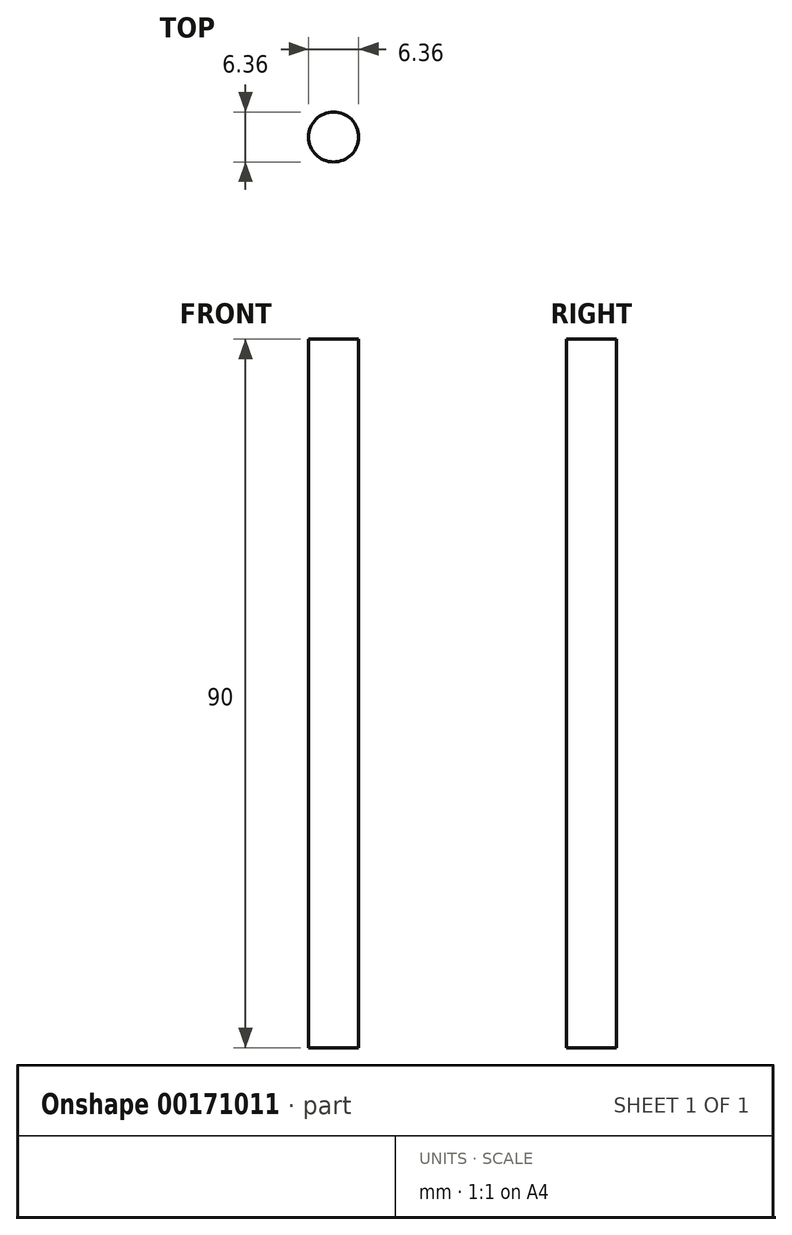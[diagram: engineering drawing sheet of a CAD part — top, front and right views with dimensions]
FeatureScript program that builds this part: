
annotation { "Feature Type Name" : "Feature", "Feature Type Description" : "" }
export const myFeature = defineFeature(function(context is Context, id is Id, definition is map)
    precondition{}
    {
        {
            var Q0;
            Q0=qCreatedBy(makeId("Top.planeOp"),FACE);
            var sketch = newSketch(context, id + "F0", { "sketchPlane" : qUnion([Q0])});
            skCircle(sketch, "E0", {"center": v(0, 0) * mm, "radius": 3.17 * mm});
            skSolve(sketch);
        }
        {
            var Q0;
            Q0=makeQuery(id+"F0.imprint","IMPRINT",FACE,{"disambiguationData":[TD([[makeQuery(id+"F0.imprint","IMPRINT",EDGE,{"derivedFrom":sQuery(id+"F0.wireOp",EDGE,"E0")}),1.0]])]});
            extrude(context, id + "F1", {"entities" : qUnion([Q0]), "depth" : 90 * mm});
        }
    });
